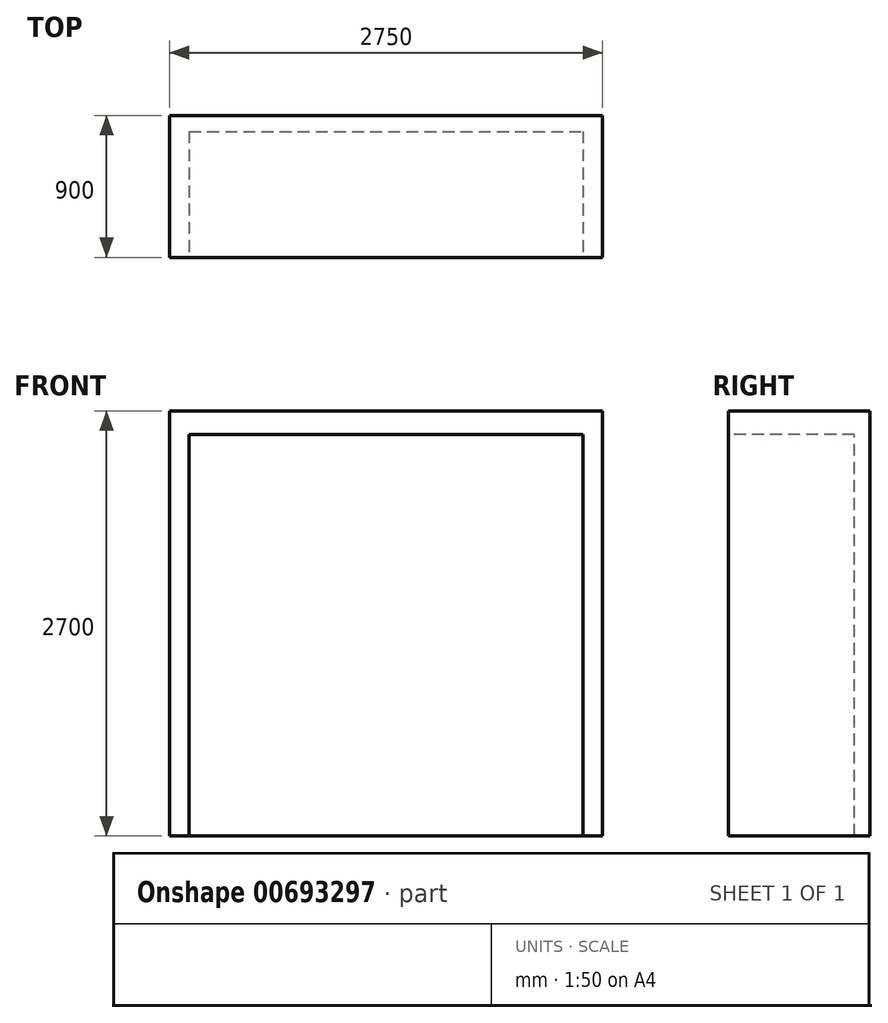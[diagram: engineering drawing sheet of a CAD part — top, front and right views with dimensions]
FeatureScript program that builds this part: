
annotation { "Feature Type Name" : "Feature", "Feature Type Description" : "" }
export const myFeature = defineFeature(function(context is Context, id is Id, definition is map)
    precondition{}
    {
        {
            var Q0;
            Q0=qCreatedBy(makeId("Top.planeOp"),FACE);
            var sketch = newSketch(context, id + "F0", { "sketchPlane" : qUnion([Q0])});
            skLineSegment(sketch, "E0.bottom", {"start": v(-1375, 450) * mm, "end": v(1375, 450) * mm});
            skLineSegment(sketch, "E0.top", {"start": v(-1375, -450) * mm, "end": v(1375, -450) * mm});
            skLineSegment(sketch, "E0.left", {"start": v(-1375, 450) * mm, "end": v(-1375, -450) * mm});
            skLineSegment(sketch, "E0.right", {"start": v(1375, 450) * mm, "end": v(1375, -450) * mm});
            skPoint(sketch, "E0.middle", {"position": v(0, 0) * mm});
            skSolve(sketch);
        }
        {
            var Q0;
            Q0 = qSketchRegion(id + "F0", true);
            extrude(context, id + "F1", {"entities" : qUnion([Q0]), "depth" : 2700 * mm, "offsetDistance" : 25 * mm});
        }
        {
            var Q0;
            Q0=makeQuery(id+"F1.opExtrude","SWEPT_FACE",FACE,{"disambiguationData":[OSD([sQuery(id+"F0.wireOp",EDGE,"E0.top")])]});
            var sketch = newSketch(context, id + "F2", { "sketchPlane" : qUnion([Q0])});
            skLineSegment(sketch, "E1", {"start": v(-1250, 0) * mm, "end": v(-1250, 2550) * mm});
            skLineSegment(sketch, "E2", {"start": v(-1250, 2550) * mm, "end": v(1250, 2550) * mm});
            skLineSegment(sketch, "E3", {"start": v(1250, 2550) * mm, "end": v(1250, 0) * mm});
            skLineSegment(sketch, "E4", {"start": v(-1250, 0) * mm, "end": v(1250, 0) * mm});
            skSolve(sketch);
        }
        {
            var Q0;
            Q0=makeQuery(id+"F2.imprint","IMPRINT",FACE,{"disambiguationData":[TD([[makeQuery(id+"F2.imprint","IMPRINT",EDGE,{"derivedFrom":sQuery(id+"F2.wireOp",EDGE,"E1")}),-1.0]])]});
            extrude(context, id + "F3", {"entities" : qUnion([Q0]), "operationType" : NewBodyOperationType.REMOVE, "oppositeDirection" : true, "depth" : 800 * mm, "offsetDistance" : 25 * mm});
        }
    });
